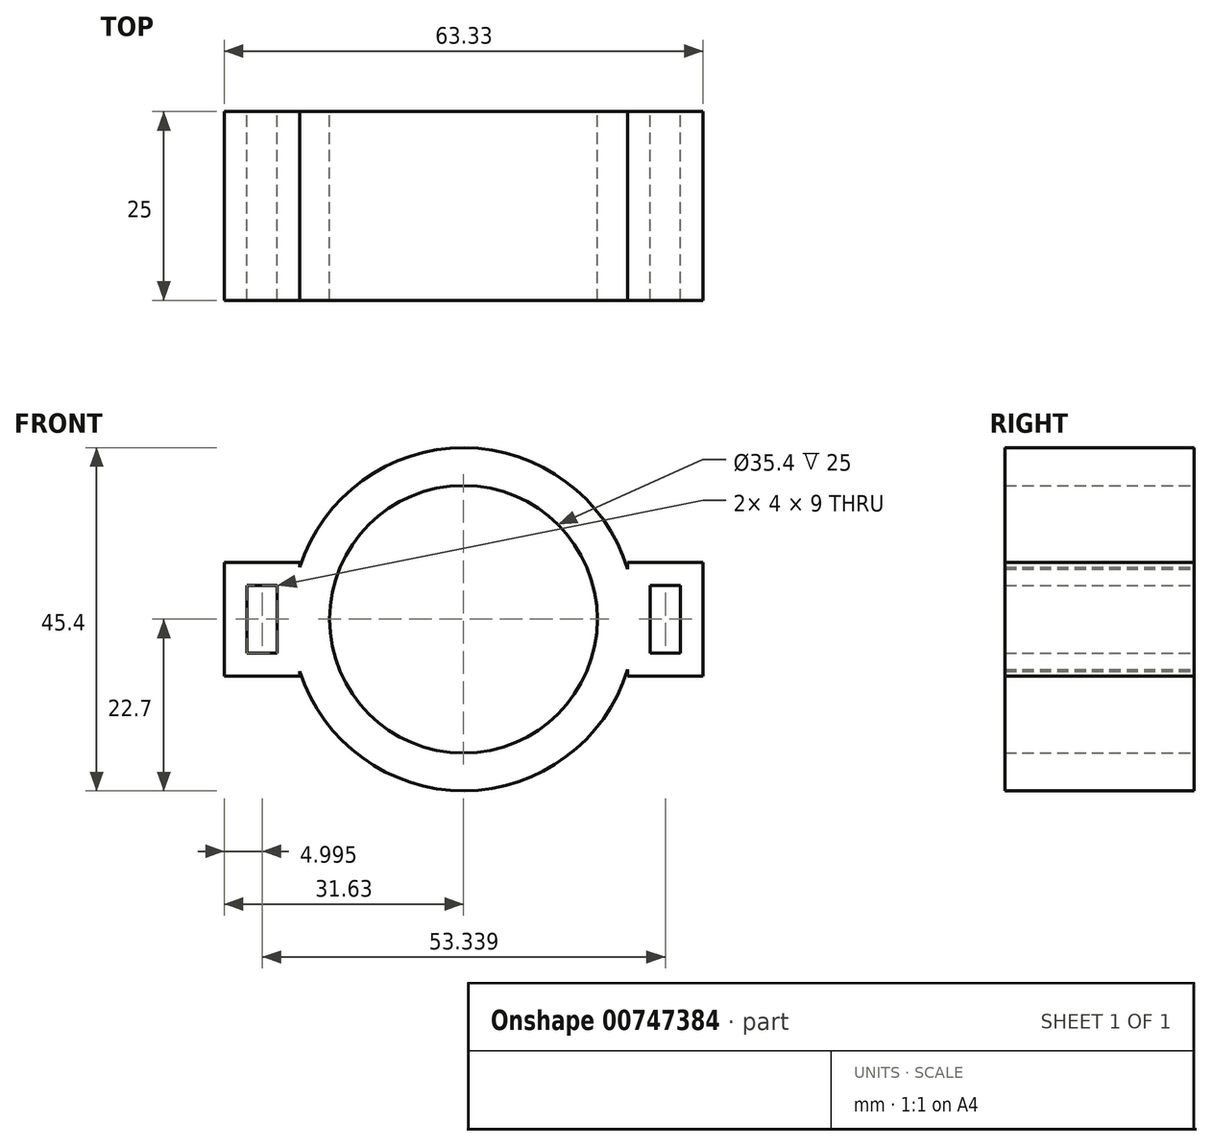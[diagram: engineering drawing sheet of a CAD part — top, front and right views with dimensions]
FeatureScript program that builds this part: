
annotation { "Feature Type Name" : "Feature", "Feature Type Description" : "" }
export const myFeature = defineFeature(function(context is Context, id is Id, definition is map)
    precondition{}
    {
        {
            var Q0;
            Q0=qCreatedBy(makeId("Front.planeOp"),FACE);
            var sketch = newSketch(context, id + "F0", { "sketchPlane" : qUnion([Q0])});
            skCircle(sketch, "E0", {"center": v(0, 0) * mm, "radius": 17.7 * mm});
            skCircle(sketch, "E1.0", {"center": v(0, 0) * mm, "radius": 22.7 * mm});
            skSolve(sketch);
        }
        {
            var Q0;
            Q0=makeQuery(id+"F0.imprint","IMPRINT",FACE,{"disambiguationData":[TD([[makeQuery(id+"F0.imprint","IMPRINT",EDGE,{"derivedFrom":sQuery(id+"F0.wireOp",EDGE,"E0")}),-1.0]])]});
            extrude(context, id + "F1", {"entities" : qUnion([Q0]), "depth" : 25 * mm, "offsetDistance" : 25 * mm});
        }
        {
            var Q0;
            Q0=qCreatedBy(makeId("Front.planeOp"),FACE);
            var sketch = newSketch(context, id + "F2", { "sketchPlane" : qUnion([Q0])});
            skLineSegment(sketch, "E2.bottom", {"start": v(-21.63, -7.5) * mm, "end": v(-31.63, -7.5) * mm});
            skLineSegment(sketch, "E2.top", {"start": v(-21.63, 7.5) * mm, "end": v(-31.63, 7.5) * mm});
            skLineSegment(sketch, "E2.left", {"start": v(-21.63, -7.5) * mm, "end": v(-21.63, 7.5) * mm});
            skLineSegment(sketch, "E2.right", {"start": v(-31.63, -7.5) * mm, "end": v(-31.63, 7.5) * mm});
            skPoint(sketch, "E2.middle", {"position": v(-26.63, 0) * mm});
            skLineSegment(sketch, "E3.bottom", {"start": v(31.7, -7.5) * mm, "end": v(21.7, -7.5) * mm});
            skLineSegment(sketch, "E3.top", {"start": v(31.7, 7.5) * mm, "end": v(21.7, 7.5) * mm});
            skLineSegment(sketch, "E3.left", {"start": v(31.7, -7.5) * mm, "end": v(31.7, 7.5) * mm});
            skLineSegment(sketch, "E3.right", {"start": v(21.7, -7.5) * mm, "end": v(21.7, 7.5) * mm});
            skPoint(sketch, "E3.middle", {"position": v(26.7, 0) * mm});
            skLineSegment(sketch, "E4.0", {"start": v(-24.63, 4.5) * mm, "end": v(-28.63, 4.5) * mm});
            skLineSegment(sketch, "E4.1", {"start": v(-24.63, -4.5) * mm, "end": v(-24.63, 4.5) * mm});
            skLineSegment(sketch, "E4.2", {"start": v(-24.63, -4.5) * mm, "end": v(-28.63, -4.5) * mm});
            skLineSegment(sketch, "E4.3", {"start": v(-28.63, -4.5) * mm, "end": v(-28.63, 4.5) * mm});
            skLineSegment(sketch, "E5.0", {"start": v(28.7, 4.5) * mm, "end": v(24.7, 4.5) * mm});
            skLineSegment(sketch, "E5.1", {"start": v(28.7, -4.5) * mm, "end": v(28.7, 4.5) * mm});
            skLineSegment(sketch, "E5.2", {"start": v(28.7, -4.5) * mm, "end": v(24.7, -4.5) * mm});
            skLineSegment(sketch, "E5.3", {"start": v(24.7, -4.5) * mm, "end": v(24.7, 4.5) * mm});
            skSolve(sketch);
        }
        {
            var Q0;
            Q0 = qSketchRegion(id + "F2", true);
            extrude(context, id + "F3", {"entities" : qUnion([Q0]), "operationType" : NewBodyOperationType.ADD, "depth" : 25 * mm, "offsetDistance" : 25 * mm});
        }
    });
